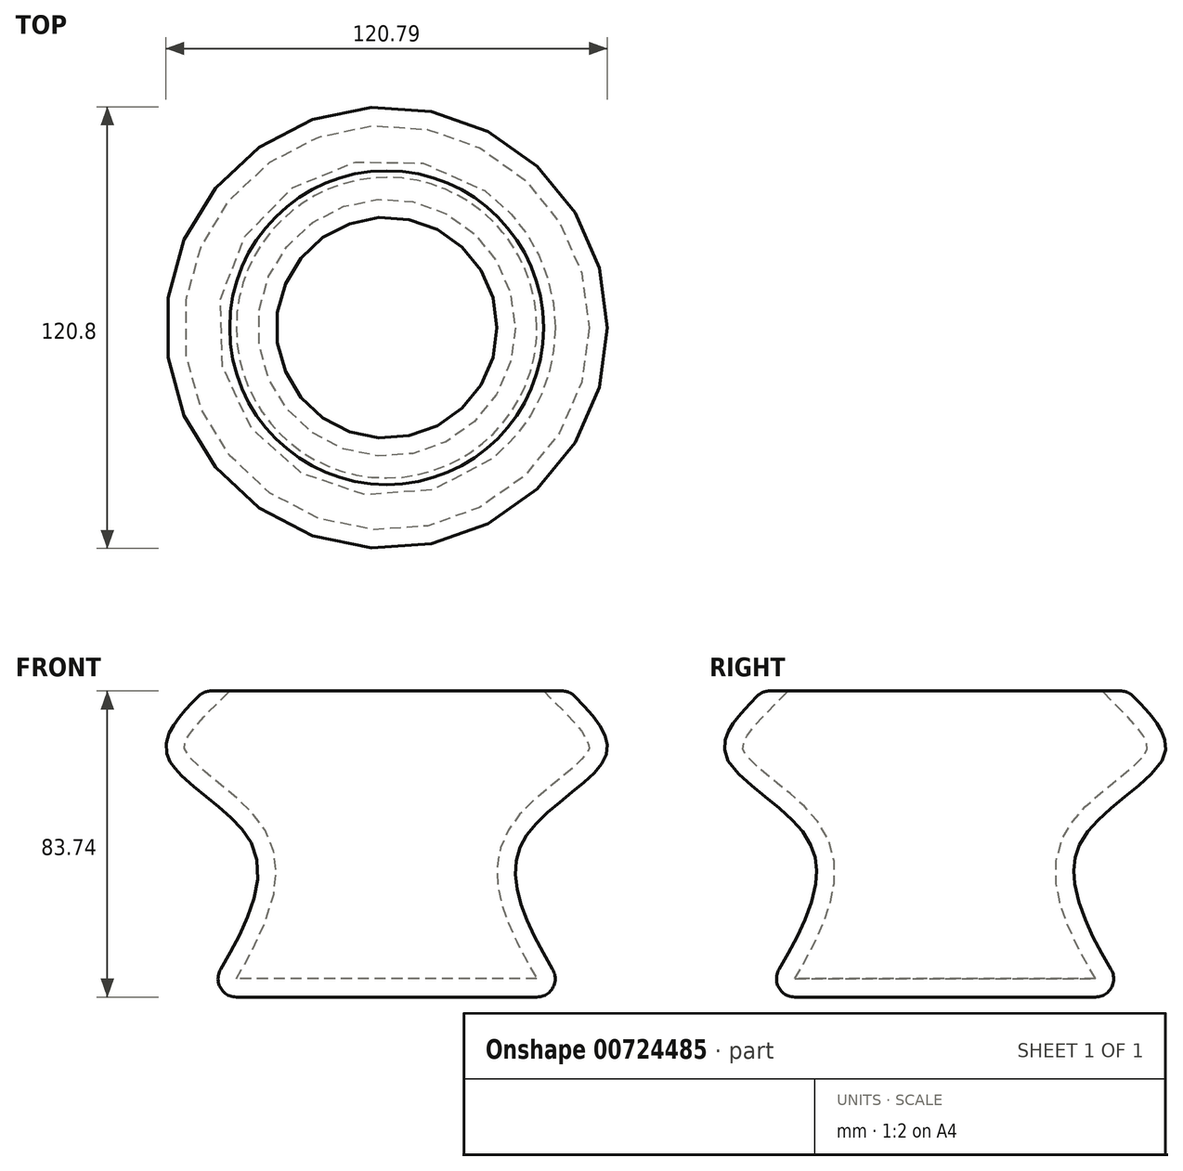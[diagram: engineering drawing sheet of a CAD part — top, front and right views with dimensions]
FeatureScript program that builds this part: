
annotation { "Feature Type Name" : "Feature", "Feature Type Description" : "" }
export const myFeature = defineFeature(function(context is Context, id is Id, definition is map)
    precondition{}
    {
        {
            var Q0;
            Q0=qCreatedBy(makeId("Right.planeOp"),FACE);
            var sketch = newSketch(context, id + "F0", { "sketchPlane" : qUnion([Q0])});
            skLineSegment(sketch, "E0", {"start": v(0, 56.36) * mm, "end": v(0, -23) * mm, "construction": true});
            skLineSegment(sketch, "E1", {"start": v(0, 42.14) * mm, "end": v(0, -41.6) * mm});
            skLineSegment(sketch, "E2", {"start": v(0, -41.6) * mm, "end": v(50, -41.6) * mm});
            skLineSegment(sketch, "E3", {"start": v(0, 42.14) * mm, "end": v(50, 42.14) * mm});
            skFitSpline(sketch, "E4", {"points": [v(50, 42.14) * mm, v(59.99, 24.36) * mm, v(36.75, 0) * mm, v(50, -41.6) * mm], "startDerivative": vector(67.65, -67.55) * mm, "endDerivative": vector(71.35, -116.32) * mm});
            skSolve(sketch);
        }
        {
            var Q0;
            Q0=makeQuery(id+"F0.imprint","IMPRINT",FACE,{"disambiguationData":[TD([[makeQuery(id+"F0.imprint","IMPRINT",EDGE,{"derivedFrom":sQuery(id+"F0.wireOp",EDGE,"E1")}),1.0]])]});
            var Q1;
            Q1=sQuery(id+"F0.wireOp",EDGE,"E0");
            revolve(context, id + "F1", {"surfaceOperationType" : NewSurfaceOperationType.NEW, "entities" : qUnion([Q0]), "axis" : qUnion([Q1]), "revolveType" : RevolveType.FULL});
        }
        {
            var Q0;
            Q0=makeQuery(id+"F1.opRevolve","SWEPT_FACE",FACE,{"disambiguationData":[OSD([sQuery(id+"F0.wireOp",EDGE,"E3")])]});
            shell(context, id + "F2", {"entities" : qUnion([Q0]), "thickness" : 5 * mm});
        }
        {
            var Q0;
            Q0=makeQuery(id+"F1.opRevolve","SWEPT_EDGE",EDGE,{"disambiguationData":[OSD([sQuery(id+"F0.wireOp",EDGE,"E3"),sQuery(id+"F0.wireOp",EDGE,"ImYWDLZ9-jlOa-acaG-oCu2-IU9uCunWx7Nh")])]});
            var Q1;
            Q1=makeQuery(id+"F1.opRevolve","SWEPT_EDGE",EDGE,{"disambiguationData":[OSD([sQuery(id+"F0.wireOp",EDGE,"E2"),sQuery(id+"F0.wireOp",EDGE,"ImYWDLZ9-jlOa-acaG-oCu2-IU9uCunWx7Nh")])]});
            fillet(context, id + "F3", {"entities" : qUnion([Q0, Q1]), "radius" : 5 * mm, "tangentPropagation" : true, "allowEdgeOverflow" : false});
        }
    });
